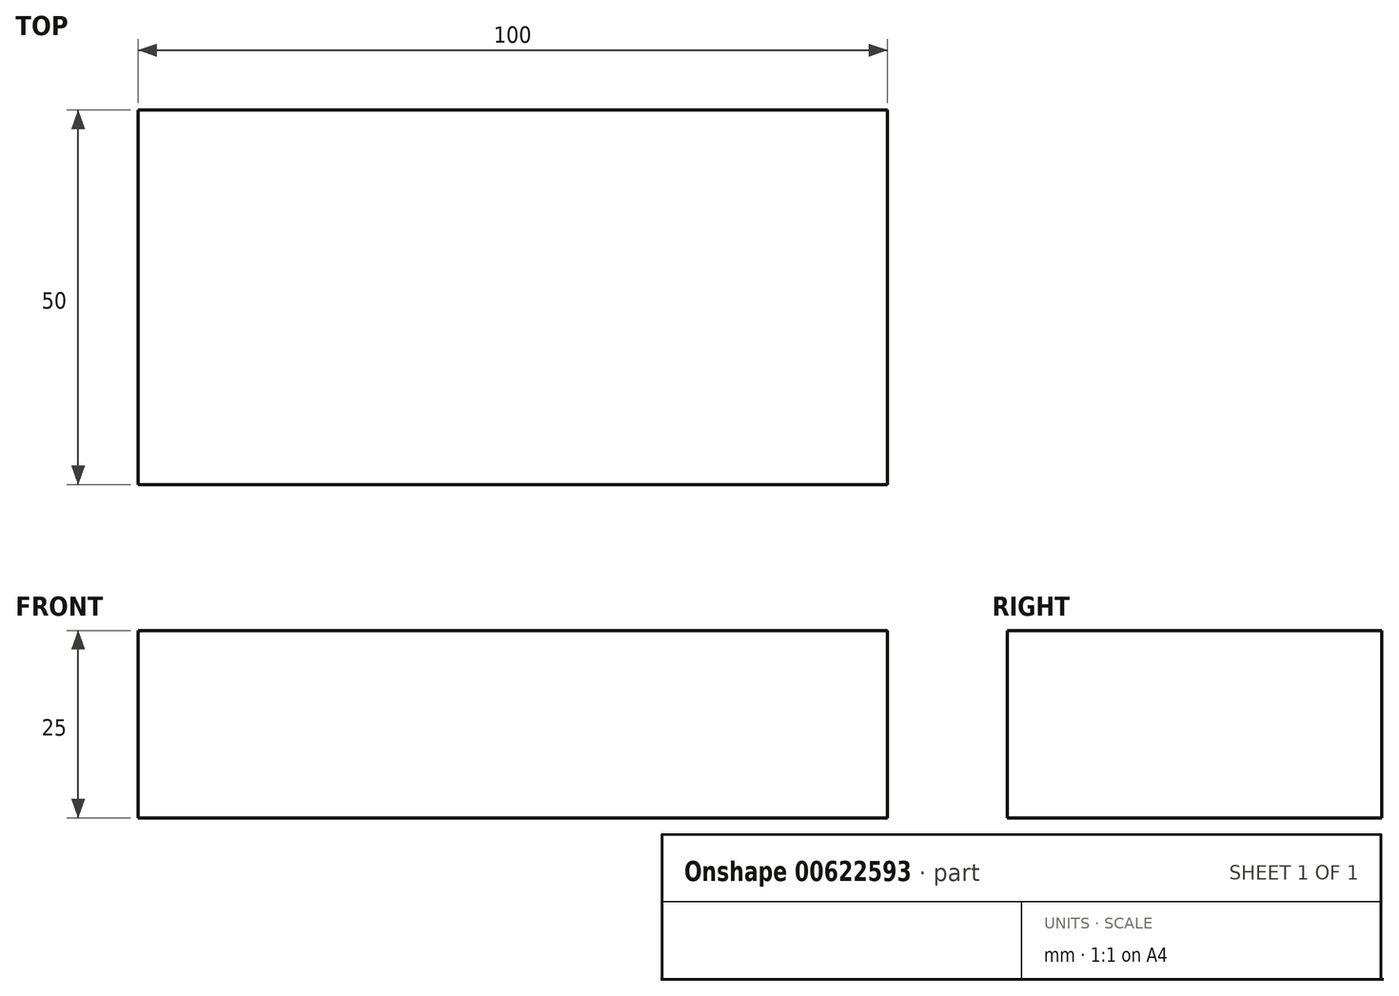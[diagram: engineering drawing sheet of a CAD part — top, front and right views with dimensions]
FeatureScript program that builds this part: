
annotation { "Feature Type Name" : "Feature", "Feature Type Description" : "" }
export const myFeature = defineFeature(function(context is Context, id is Id, definition is map)
    precondition{}
    {
        {
            var Q0;
            Q0=qCreatedBy(makeId("Top.planeOp"),FACE);
            var sketch = newSketch(context, id + "F0", { "sketchPlane" : qUnion([Q0])});
            skLineSegment(sketch, "E0.bottom", {"start": v(0, 0) * mm, "end": v(100, 0) * mm});
            skLineSegment(sketch, "E0.left", {"start": v(0, 0) * mm, "end": v(0, 50) * mm});
            skLineSegment(sketch, "E0.right", {"start": v(100, 0) * mm, "end": v(100, 50) * mm});
            skLineSegment(sketch, "E1", {"start": v(0, 50) * mm, "end": v(100, 50) * mm});
            skSolve(sketch);
        }
        {
            var Q0;
            Q0 = qSketchRegion(id + "F0", true);
            extrude(context, id + "F1", {"entities" : qUnion([Q0]), "depth" : 25 * mm, "offsetDistance" : 25 * mm});
        }
    });
